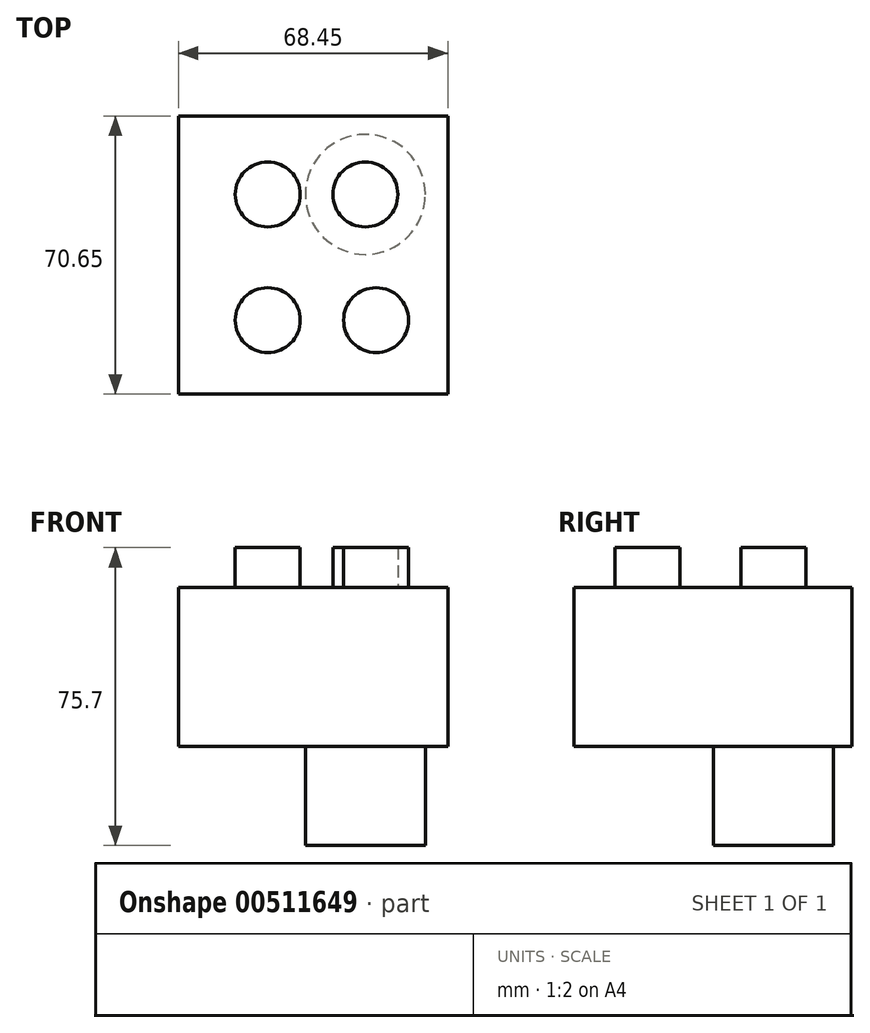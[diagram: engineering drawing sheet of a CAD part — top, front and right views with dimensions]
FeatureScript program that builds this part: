
annotation { "Feature Type Name" : "Feature", "Feature Type Description" : "" }
export const myFeature = defineFeature(function(context is Context, id is Id, definition is map)
    precondition{}
    {
        {
            var Q0;
            Q0=qCreatedBy(makeId("Top.planeOp"),FACE);
            var sketch = newSketch(context, id + "F0", { "sketchPlane" : qUnion([Q0])});
            skLineSegment(sketch, "E0.bottom", {"start": v(-22.71, 40.76) * mm, "end": v(45.74, 40.76) * mm});
            skLineSegment(sketch, "E0.top", {"start": v(-22.71, -29.89) * mm, "end": v(45.74, -29.89) * mm});
            skLineSegment(sketch, "E0.left", {"start": v(-22.71, 40.76) * mm, "end": v(-22.71, -29.89) * mm});
            skLineSegment(sketch, "E0.right", {"start": v(45.74, 40.76) * mm, "end": v(45.74, -29.89) * mm});
            skSolve(sketch);
        }
        {
            var Q0;
            Q0 = qSketchRegion(id + "F0", true);
            extrude(context, id + "F1", {"entities" : qUnion([Q0]), "depth" : 40.4 * mm});
        }
        {
            var Q0;
            Q0=makeQuery(id+"F1.opExtrude","CAP_FACE",FACE,{"disambiguationData":[OSD([sQuery(id+"F0.wireOp",EDGE,"E0.bottom"),sQuery(id+"F0.wireOp",EDGE,"E0.top"),sQuery(id+"F0.wireOp",EDGE,"E0.left"),sQuery(id+"F0.wireOp",EDGE,"E0.right")])],"isStart":false});
            var sketch = newSketch(context, id + "F2", { "sketchPlane" : qUnion([Q0])});
            skCircle(sketch, "E1", {"center": v(24.8, 20.84) * mm, "radius": 15.24 * mm});
            skSolve(sketch);
        }
        {
            var Q0;
            Q0 = qSketchRegion(id + "F2", true);
            extrude(context, id + "F3", {"entities" : qUnion([Q0]), "operationType" : NewBodyOperationType.ADD, "oppositeDirection" : true, "depth" : 65.53 * mm});
        }
        {
            var Q0;
            Q0=makeQuery(id+"F3.boolean.opBoolean","MERGE",FACE,{"derivedFrom":[makeQuery(id+"F1.opExtrude","CAP_FACE",FACE,{"disambiguationData":[OSD([sQuery(id+"F0.wireOp",EDGE,"E0.bottom"),sQuery(id+"F0.wireOp",EDGE,"E0.top"),sQuery(id+"F0.wireOp",EDGE,"E0.left"),sQuery(id+"F0.wireOp",EDGE,"E0.right")])],"isStart":false}),makeQuery(id+"F3.opExtrude","CAP_FACE",FACE,{"disambiguationData":[OSD([sQuery(id+"F2.wireOp",EDGE,"E1")])],"isStart":true})]});
            var sketch = newSketch(context, id + "F4", { "sketchPlane" : qUnion([Q0])});
            skCircle(sketch, "E2", {"center": v(27.53, -11.12) * mm, "radius": 8.26 * mm});
            skCircle(sketch, "E3", {"center": v(0, -11.12) * mm, "radius": 8.26 * mm});
            skCircle(sketch, "E4", {"center": v(24.8, 20.84) * mm, "radius": 8.26 * mm});
            skCircle(sketch, "E5", {"center": v(0, 20.84) * mm, "radius": 8.26 * mm});
            skSolve(sketch);
        }
        {
            var Q0;
            Q0=makeQuery(id+"F4.imprint","IMPRINT",FACE,{"disambiguationData":[TD([[makeQuery(id+"F4.imprint","IMPRINT",EDGE,{"derivedFrom":sQuery(id+"F4.wireOp",EDGE,"E5")}),1.0]])]});
            var Q1;
            Q1=makeQuery(id+"F4.imprint","IMPRINT",FACE,{"disambiguationData":[TD([[makeQuery(id+"F4.imprint","IMPRINT",EDGE,{"derivedFrom":sQuery(id+"F4.wireOp",EDGE,"E3")}),1.0]])]});
            var Q2;
            Q2=makeQuery(id+"F4.imprint","IMPRINT",FACE,{"disambiguationData":[TD([[makeQuery(id+"F4.imprint","IMPRINT",EDGE,{"derivedFrom":sQuery(id+"F4.wireOp",EDGE,"E4")}),1.0]])]});
            var Q3;
            Q3=makeQuery(id+"F4.imprint","IMPRINT",FACE,{"disambiguationData":[TD([[makeQuery(id+"F4.imprint","IMPRINT",EDGE,{"derivedFrom":sQuery(id+"F4.wireOp",EDGE,"E2")}),1.0]])]});
            extrude(context, id + "F5", {"entities" : qUnion([Q0, Q1, Q2, Q3]), "operationType" : NewBodyOperationType.ADD, "depth" : 10.16 * mm, "offsetDistance" : 25.4 * mm});
        }
    });
